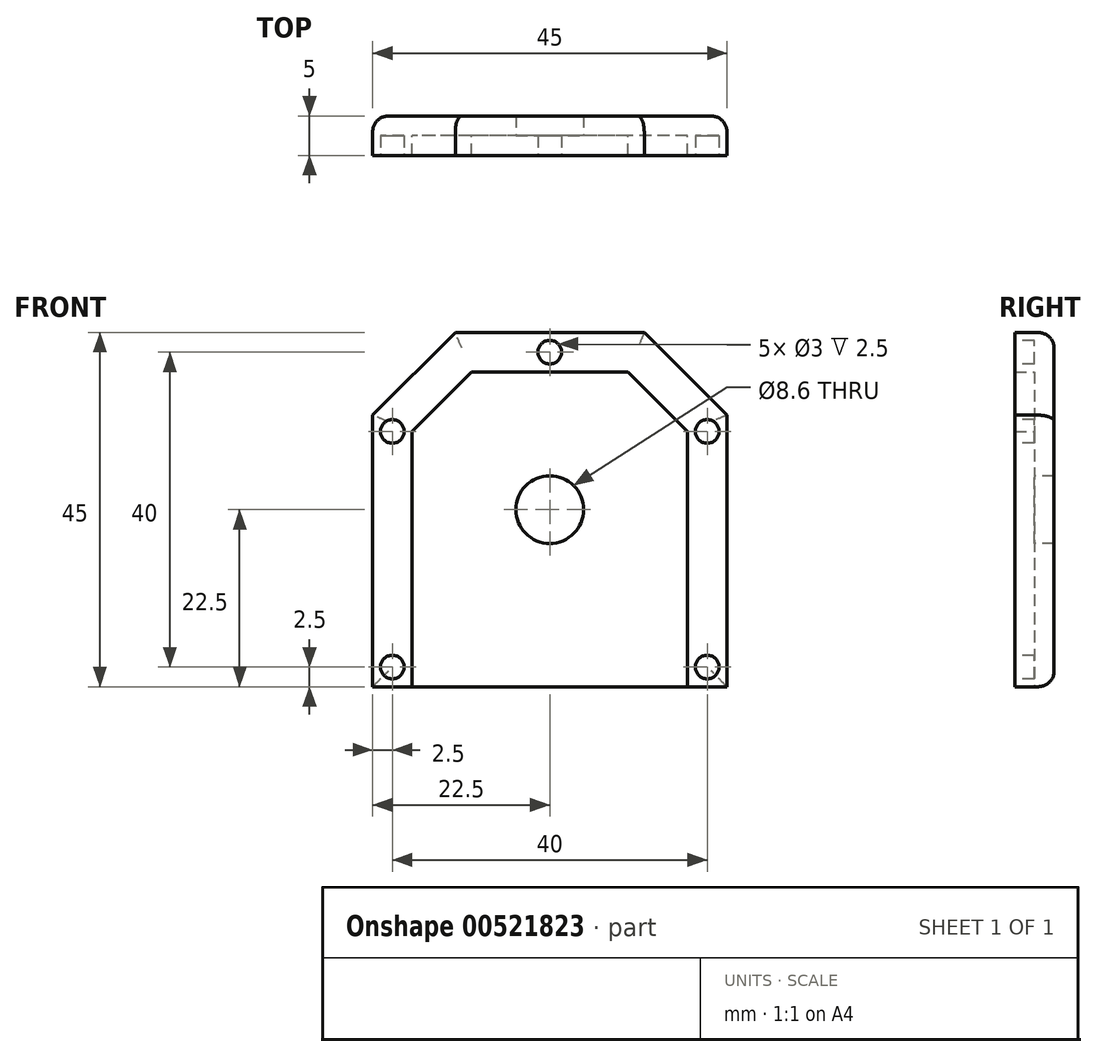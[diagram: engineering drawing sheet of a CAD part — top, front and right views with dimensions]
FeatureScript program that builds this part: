
annotation { "Feature Type Name" : "Feature", "Feature Type Description" : "" }
export const myFeature = defineFeature(function(context is Context, id is Id, definition is map)
    precondition{}
    {
        {
            var Q0;
            Q0=qCreatedBy(makeId("Front.planeOp"),FACE);
            var sketch = newSketch(context, id + "F0", { "sketchPlane" : qUnion([Q0])});
            skLineSegment(sketch, "E0.bottom", {"start": v(22.5, 22.5) * mm, "end": v(-22.5, 22.5) * mm});
            skLineSegment(sketch, "E0.top", {"start": v(22.5, -22.5) * mm, "end": v(-22.5, -22.5) * mm});
            skLineSegment(sketch, "E0.left", {"start": v(22.5, 22.5) * mm, "end": v(22.5, -22.5) * mm});
            skLineSegment(sketch, "E0.right", {"start": v(-22.5, 22.5) * mm, "end": v(-22.5, -22.5) * mm});
            skPoint(sketch, "E0.middle", {"position": v(0, 0) * mm});
            skSolve(sketch);
        }
        {
            var Q0;
            Q0=makeQuery(id+"F0.imprint","IMPRINT",FACE,{"disambiguationData":[TD([[makeQuery(id+"F0.imprint","IMPRINT",EDGE,{"derivedFrom":sQuery(id+"F0.wireOp",EDGE,"E0.bottom")}),1.0]])]});
            extrude(context, id + "F1", {"entities" : qUnion([Q0]), "depth" : 2.5 * mm, "offsetDistance" : 25 * mm});
        }
        {
            var Q0;
            Q0=makeQuery(id+"F1.opExtrude","SWEPT_EDGE",EDGE,{"disambiguationData":[OSD([sQuery(id+"F0.wireOp",EDGE,"E0.bottom"),sQuery(id+"F0.wireOp",EDGE,"E0.right")])]});
            var Q1;
            Q1=makeQuery(id+"F1.opExtrude","SWEPT_EDGE",EDGE,{"disambiguationData":[OSD([sQuery(id+"F0.wireOp",EDGE,"E0.bottom"),sQuery(id+"F0.wireOp",EDGE,"E0.left")])]});
            chamfer(context, id + "F2", {"entities" : qUnion([Q0, Q1]), "width" : 10.5 * mm, "tangentPropagation" : true});
        }
        {
            var Q0;
            Q0=makeQuery(id+"F1.opExtrude","CAP_FACE",FACE,{"disambiguationData":[OSD([sQuery(id+"F0.wireOp",EDGE,"E0.bottom"),sQuery(id+"F0.wireOp",EDGE,"E0.top"),sQuery(id+"F0.wireOp",EDGE,"E0.left"),sQuery(id+"F0.wireOp",EDGE,"E0.right")])],"isStart":false});
            var sketch = newSketch(context, id + "F3", { "sketchPlane" : qUnion([Q0])});
            skLineSegment(sketch, "E1.0", {"start": v(-17.5, 9.93) * mm, "end": v(-17.5, -22.5) * mm});
            skLineSegment(sketch, "E1.1", {"start": v(17.5, 9.93) * mm, "end": v(17.5, -22.5) * mm});
            skLineSegment(sketch, "E1.2", {"start": v(17.5, 9.93) * mm, "end": v(9.93, 17.5) * mm});
            skLineSegment(sketch, "E1.3", {"start": v(9.93, 17.5) * mm, "end": v(-9.93, 17.5) * mm});
            skLineSegment(sketch, "E1.4", {"start": v(-9.93, 17.5) * mm, "end": v(-17.5, 9.93) * mm});
            skCircle(sketch, "E2", {"center": v(0, 0) * mm, "radius": 4.3 * mm});
            skSolve(sketch);
        }
        {
            var Q0;
            {var subQ7=sQuery(id+"F3.wireOp",EDGE,"E1.0");Q0=makeQuery(id+"F3.imprint","IMPRINT",FACE,{"disambiguationData":[TD([[makeQuery(id+"F3.imprint","IMPRINT",EDGE,{"derivedFrom":subQ7}),-1.0]])]});}
            extrude(context, id + "F4", {"entities" : qUnion([Q0]), "operationType" : NewBodyOperationType.ADD, "depth" : 2.5 * mm, "offsetDistance" : 25 * mm});
        }
        {
            var Q0;
            Q0=makeQuery(id+"F1.opExtrude","CAP_FACE",FACE,{"disambiguationData":[OSD([sQuery(id+"F0.wireOp",EDGE,"E0.bottom"),sQuery(id+"F0.wireOp",EDGE,"E0.top"),sQuery(id+"F0.wireOp",EDGE,"E0.left"),sQuery(id+"F0.wireOp",EDGE,"E0.right")])],"isStart":true});
            fillet(context, id + "F5", {"entities" : qUnion([Q0]), "radius" : 2 * mm, "tangentPropagation" : true, "allowEdgeOverflow" : false});
        }
        {
            var Q0;
            Q0=makeQuery(id+"F3.imprint","IMPRINT",FACE,{"disambiguationData":[TD([[makeQuery(id+"F3.imprint","IMPRINT",EDGE,{"derivedFrom":sQuery(id+"F3.wireOp",EDGE,"E2")}),1.0]])]});
            extrude(context, id + "F6", {"entities" : qUnion([Q0]), "operationType" : NewBodyOperationType.REMOVE, "oppositeDirection" : true, "depth" : 25 * mm, "offsetDistance" : 25 * mm});
        }
        {
            var Q0;
            Q0=makeQuery(id+"F4.opExtrude","CAP_FACE",FACE,{"disambiguationData":[OSD([sQuery(id+"F0.wireOp",EDGE,"E0.bottom"),sQuery(id+"F0.wireOp",EDGE,"E0.top"),sQuery(id+"F0.wireOp",EDGE,"E0.left"),sQuery(id+"F0.wireOp",EDGE,"E0.right"),sQuery(id+"F3.wireOp",EDGE,"E1.0"),sQuery(id+"F3.wireOp",EDGE,"E1.1"),sQuery(id+"F3.wireOp",EDGE,"E1.2"),sQuery(id+"F3.wireOp",EDGE,"E1.3"),sQuery(id+"F3.wireOp",EDGE,"E1.4")])],"isStart":false});
            var sketch = newSketch(context, id + "F7", { "sketchPlane" : qUnion([Q0])});
            skLineSegment(sketch, "E3.0", {"start": v(-17.5, 9.93) * mm, "end": v(-17.5, -22.5) * mm});
            skLineSegment(sketch, "E3.1", {"start": v(17.5, 9.93) * mm, "end": v(17.5, -22.5) * mm});
            skLineSegment(sketch, "E3.2", {"start": v(17.5, 9.93) * mm, "end": v(9.93, 17.5) * mm});
            skLineSegment(sketch, "E3.3", {"start": v(9.93, 17.5) * mm, "end": v(-9.93, 17.5) * mm});
            skLineSegment(sketch, "E3.4", {"start": v(-9.93, 17.5) * mm, "end": v(-17.5, 9.93) * mm});
            skLineSegment(sketch, "E4.bottom", {"start": v(-22.5, -22.5) * mm, "end": v(-20, -22.5) * mm});
            skLineSegment(sketch, "E4.top", {"start": v(-22.5, -20) * mm, "end": v(-20, -20) * mm});
            skLineSegment(sketch, "E4.left", {"start": v(-22.5, -22.5) * mm, "end": v(-22.5, -20) * mm});
            skLineSegment(sketch, "E4.right", {"start": v(-20, -22.5) * mm, "end": v(-20, -20) * mm});
            skLineSegment(sketch, "E5.bottom", {"start": v(17.5, -22.5) * mm, "end": v(20, -22.5) * mm});
            skLineSegment(sketch, "E5.top", {"start": v(17.5, -20) * mm, "end": v(20, -20) * mm});
            skLineSegment(sketch, "E5.left", {"start": v(17.5, -22.5) * mm, "end": v(17.5, -20) * mm});
            skLineSegment(sketch, "E5.right", {"start": v(20, -22.5) * mm, "end": v(20, -20) * mm});
            skLineSegment(sketch, "E6.bottom", {"start": v(17.5, 9.93) * mm, "end": v(20, 9.93) * mm});
            skLineSegment(sketch, "E6.top", {"start": v(17.5, 7.43) * mm, "end": v(20, 7.43) * mm});
            skLineSegment(sketch, "E6.left", {"start": v(17.5, 9.93) * mm, "end": v(17.5, 7.43) * mm});
            skLineSegment(sketch, "E6.right", {"start": v(20, 9.93) * mm, "end": v(20, 7.43) * mm});
            skLineSegment(sketch, "E7.bottom", {"start": v(-17.5, 9.93) * mm, "end": v(-20, 9.93) * mm});
            skLineSegment(sketch, "E7.top", {"start": v(-17.5, 7.43) * mm, "end": v(-20, 7.43) * mm});
            skLineSegment(sketch, "E7.left", {"start": v(-17.5, 9.93) * mm, "end": v(-17.5, 7.43) * mm});
            skLineSegment(sketch, "E7.right", {"start": v(-20, 9.93) * mm, "end": v(-20, 7.43) * mm});
            skLineSegment(sketch, "E8", {"start": v(0, 17.5) * mm, "end": v(0, 20) * mm});
            skCircle(sketch, "E9", {"center": v(-20, 9.93) * mm, "radius": 1.5 * mm});
            skCircle(sketch, "E10", {"center": v(-20, -20) * mm, "radius": 1.5 * mm});
            skCircle(sketch, "E11", {"center": v(0, 20) * mm, "radius": 1.5 * mm});
            skCircle(sketch, "E12", {"center": v(20, 9.93) * mm, "radius": 1.5 * mm});
            skCircle(sketch, "E13", {"center": v(20, -20) * mm, "radius": 1.5 * mm});
            skSolve(sketch);
        }
        {
            var Q0;
            {var subQ0=sQuery(id+"F7.wireOp",EDGE,"E5.right");var subQ1=sQuery(id+"F7.wireOp",EDGE,"E5.top");var subQ2=makeQuery(id+"F7.imprint","INTERSECT",VERTEX,{"derivedFrom":[subQ1,subQ0]});Q0=makeQuery(id+"F7.imprint","IMPRINT",FACE,{"disambiguationData":[TD([[makeQuery(id+"F7.imprint","IMPRINT",EDGE,{"disambiguationData":[TD([[subQ2,1.0]])],"derivedFrom":subQ1}),-1.0]])]});}
            var Q1;
            {var subQ0=sQuery(id+"F7.wireOp",EDGE,"E5.right");var subQ1=sQuery(id+"F7.wireOp",EDGE,"E5.top");var subQ2=makeQuery(id+"F7.imprint","INTERSECT",VERTEX,{"derivedFrom":[subQ1,subQ0]});Q1=makeQuery(id+"F7.imprint","IMPRINT",FACE,{"disambiguationData":[TD([[makeQuery(id+"F7.imprint","IMPRINT",EDGE,{"disambiguationData":[TD([[subQ2,1.0]])],"derivedFrom":subQ1}),1.0]])]});}
            var Q2;
            {var subQ0=sQuery(id+"F7.wireOp",EDGE,"E4.right");var subQ1=sQuery(id+"F7.wireOp",EDGE,"E4.top");var subQ2=makeQuery(id+"F7.imprint","INTERSECT",VERTEX,{"derivedFrom":[subQ1,subQ0]});Q2=makeQuery(id+"F7.imprint","IMPRINT",FACE,{"disambiguationData":[TD([[makeQuery(id+"F7.imprint","IMPRINT",EDGE,{"disambiguationData":[TD([[subQ2,1.0]])],"derivedFrom":subQ1}),-1.0]])]});}
            var Q3;
            {var subQ0=sQuery(id+"F7.wireOp",EDGE,"E4.right");var subQ1=sQuery(id+"F7.wireOp",EDGE,"E4.top");var subQ2=makeQuery(id+"F7.imprint","INTERSECT",VERTEX,{"derivedFrom":[subQ1,subQ0]});Q3=makeQuery(id+"F7.imprint","IMPRINT",FACE,{"disambiguationData":[TD([[makeQuery(id+"F7.imprint","IMPRINT",EDGE,{"disambiguationData":[TD([[subQ2,1.0]])],"derivedFrom":subQ1}),1.0]])]});}
            var Q4;
            {var subQ0=sQuery(id+"F7.wireOp",EDGE,"E7.right");var subQ1=sQuery(id+"F7.wireOp",EDGE,"E7.bottom");var subQ2=makeQuery(id+"F7.imprint","INTERSECT",VERTEX,{"derivedFrom":[subQ1,subQ0]});Q4=makeQuery(id+"F7.imprint","IMPRINT",FACE,{"disambiguationData":[TD([[makeQuery(id+"F7.imprint","IMPRINT",EDGE,{"disambiguationData":[TD([[subQ2,1.0]])],"derivedFrom":subQ1}),1.0]])]});}
            var Q5;
            {var subQ0=sQuery(id+"F7.wireOp",EDGE,"E7.right");var subQ1=sQuery(id+"F7.wireOp",EDGE,"E7.bottom");var subQ2=makeQuery(id+"F7.imprint","INTERSECT",VERTEX,{"derivedFrom":[subQ1,subQ0]});Q5=makeQuery(id+"F7.imprint","IMPRINT",FACE,{"disambiguationData":[TD([[makeQuery(id+"F7.imprint","IMPRINT",EDGE,{"disambiguationData":[TD([[subQ2,1.0]])],"derivedFrom":subQ1}),-1.0]])]});}
            var Q6;
            Q6=makeQuery(id+"F7.imprint","IMPRINT",FACE,{"disambiguationData":[TD([[makeQuery(id+"F7.imprint","IMPRINT",EDGE,{"derivedFrom":sQuery(id+"F7.wireOp",EDGE,"E11")}),1.0]])]});
            var Q7;
            {var subQ0=sQuery(id+"F7.wireOp",EDGE,"E6.right");var subQ1=sQuery(id+"F7.wireOp",EDGE,"E6.bottom");var subQ2=makeQuery(id+"F7.imprint","INTERSECT",VERTEX,{"derivedFrom":[subQ1,subQ0]});Q7=makeQuery(id+"F7.imprint","IMPRINT",FACE,{"disambiguationData":[TD([[makeQuery(id+"F7.imprint","IMPRINT",EDGE,{"disambiguationData":[TD([[subQ2,1.0]])],"derivedFrom":subQ1}),-1.0]])]});}
            var Q8;
            {var subQ0=sQuery(id+"F7.wireOp",EDGE,"E6.right");var subQ1=sQuery(id+"F7.wireOp",EDGE,"E6.bottom");var subQ2=makeQuery(id+"F7.imprint","INTERSECT",VERTEX,{"derivedFrom":[subQ1,subQ0]});Q8=makeQuery(id+"F7.imprint","IMPRINT",FACE,{"disambiguationData":[TD([[makeQuery(id+"F7.imprint","IMPRINT",EDGE,{"disambiguationData":[TD([[subQ2,1.0]])],"derivedFrom":subQ1}),1.0]])]});}
            extrude(context, id + "F8", {"entities" : qUnion([Q0, Q1, Q2, Q3, Q4, Q5, Q6, Q7, Q8]), "operationType" : NewBodyOperationType.REMOVE, "oppositeDirection" : true, "depth" : 2.5 * mm, "offsetDistance" : 25 * mm});
        }
    });
